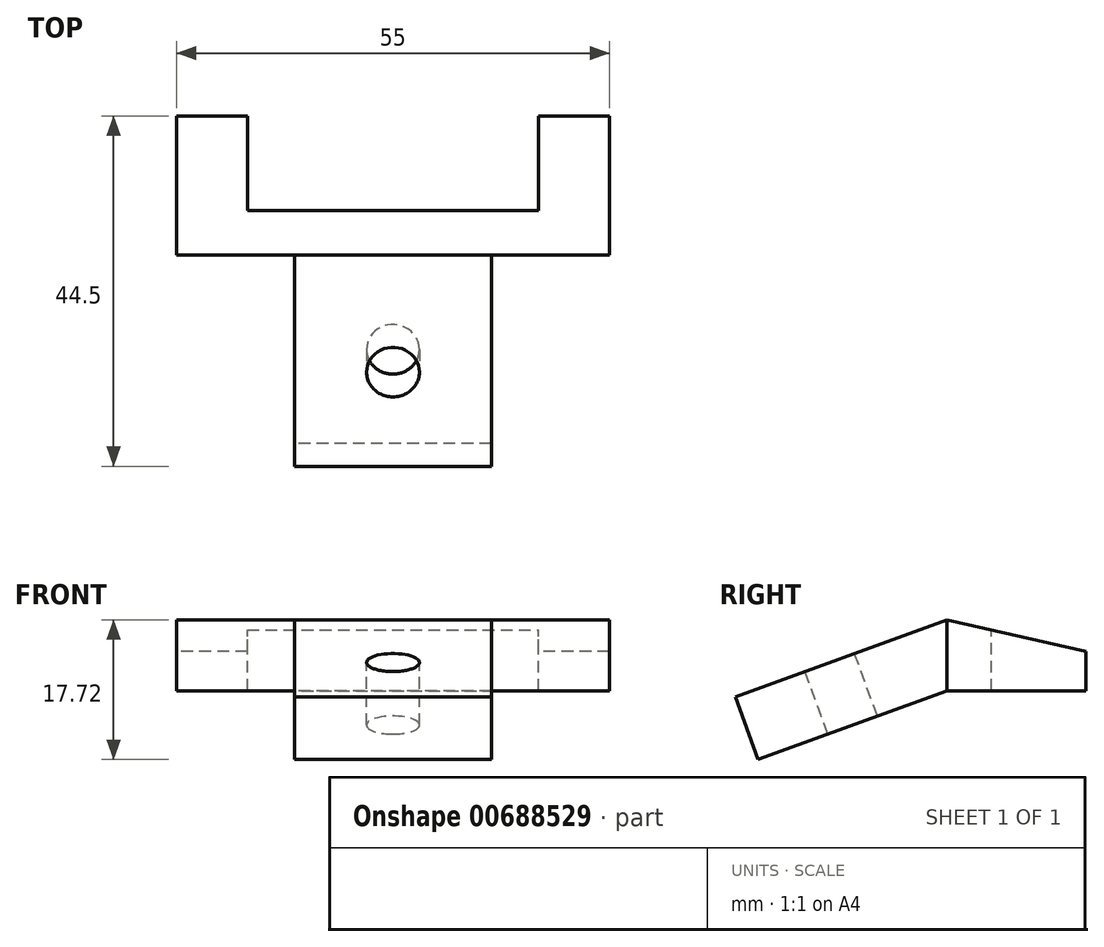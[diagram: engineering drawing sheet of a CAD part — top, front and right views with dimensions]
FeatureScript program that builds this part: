
annotation { "Feature Type Name" : "Feature", "Feature Type Description" : "" }
export const myFeature = defineFeature(function(context is Context, id is Id, definition is map)
    precondition{}
    {
        {
            var Q0;
            Q0=qCreatedBy(makeId("Right.planeOp"),FACE);
            var sketch = newSketch(context, id + "F0", { "sketchPlane" : qUnion([Q0])});
            skLineSegment(sketch, "E0", {"start": v(-3.63, 0) * mm, "end": v(14.02, 0) * mm});
            skLineSegment(sketch, "E1", {"start": v(14.02, 0) * mm, "end": v(14.02, 5) * mm});
            skLineSegment(sketch, "E2", {"start": v(14.02, 5) * mm, "end": v(-3.63, 9) * mm});
            skLineSegment(sketch, "E3", {"start": v(-27.59, -8.72) * mm, "end": v(-3.63, 0) * mm});
            skLineSegment(sketch, "E4", {"start": v(-27.59, -8.72) * mm, "end": v(-30.48, -0.77) * mm});
            skLineSegment(sketch, "E5", {"start": v(-30.48, -0.77) * mm, "end": v(-3.63, 9) * mm});
            skLineSegment(sketch, "E6", {"start": v(-27.59, -8.72) * mm, "end": v(-15.6, -4.36) * mm});
            skLineSegment(sketch, "E7", {"start": v(-15.6, -4.36) * mm, "end": v(-18.5, 3.59) * mm});
            skLineSegment(sketch, "E8", {"start": v(-3.63, 0) * mm, "end": v(-3.63, 9) * mm});
            skLineSegment(sketch, "E9.0", {"start": v(2.02, 0) * mm, "end": v(2.02, 7.72) * mm});
            skSolve(sketch);
        }
        {
            var Q0;
            {var subQ0=sQuery(id+"F0.wireOp",EDGE,"E1");Q0=makeQuery(id+"F0.imprint","IMPRINT",FACE,{"disambiguationData":[TD([[makeQuery(id+"F0.imprint","IMPRINT",EDGE,{"derivedFrom":subQ0}),1.0]])]});}
            var Q1;
            {var subQ0=sQuery(id+"F0.wireOp",EDGE,"E8");Q1=makeQuery(id+"F0.imprint","IMPRINT",FACE,{"disambiguationData":[TD([[makeQuery(id+"F0.imprint","IMPRINT",EDGE,{"derivedFrom":subQ0}),-1.0]])]});}
            extrude(context, id + "F1", {"entities" : qUnion([Q0, Q1]), "endBound" : BoundingType.SYMMETRIC, "depth" : 55 * mm, "offsetDistance" : 25 * mm});
        }
        {
            var Q0;
            Q0=makeQuery(id+"F0.imprint","IMPRINT",FACE,{"disambiguationData":[TD([[makeQuery(id+"F0.imprint","IMPRINT",EDGE,{"derivedFrom":sQuery(id+"F0.wireOp",EDGE,"E3")}),1.0]])]});
            var Q1;
            {var subQ0=sQuery(id+"F0.wireOp",EDGE,"E4");Q1=makeQuery(id+"F0.imprint","IMPRINT",FACE,{"disambiguationData":[TD([[makeQuery(id+"F0.imprint","IMPRINT",EDGE,{"derivedFrom":subQ0}),-1.0]])]});}
            extrude(context, id + "F2", {"entities" : qUnion([Q0, Q1]), "operationType" : NewBodyOperationType.ADD, "endBound" : BoundingType.SYMMETRIC, "depth" : 25 * mm, "offsetDistance" : 25 * mm});
        }
        {
            var Q0;
            {var subQ0=sQuery(id+"F0.wireOp",EDGE,"E1");Q0=makeQuery(id+"F0.imprint","IMPRINT",FACE,{"disambiguationData":[TD([[makeQuery(id+"F0.imprint","IMPRINT",EDGE,{"derivedFrom":subQ0}),1.0]])]});}
            extrude(context, id + "F3", {"entities" : qUnion([Q0]), "operationType" : NewBodyOperationType.REMOVE, "endBound" : BoundingType.SYMMETRIC, "oppositeDirection" : true, "depth" : 37 * mm, "offsetDistance" : 25 * mm});
        }
        {
            var Q0;
            Q0=makeQuery(id+"F2.opExtrude","SWEPT_FACE",FACE,{"disambiguationData":[OSD([sQuery(id+"F0.wireOp",EDGE,"E5")])]});
            var sketch = newSketch(context, id + "F4", { "sketchPlane" : qUnion([Q0])});
            skCircle(sketch, "E10", {"center": v(0, -16.16) * mm, "radius": 3.35 * mm});
            skSolve(sketch);
        }
        {
            var Q0;
            Q0=makeQuery(id+"F4.imprint","IMPRINT",FACE,{"disambiguationData":[TD([[makeQuery(id+"F4.imprint","IMPRINT",EDGE,{"derivedFrom":sQuery(id+"F4.wireOp",EDGE,"E10")}),1.0]])]});
            var Q1;
            Q1=sQuery(id+"F4.wireOp",EDGE,"E10");
            extrude(context, id + "F5", {"entities" : qUnion([Q0]), "operationType" : NewBodyOperationType.REMOVE, "surfaceEntities" : qUnion([Q1]), "endBound" : BoundingType.UP_TO_NEXT, "oppositeDirection" : true, "depth" : 25 * mm, "offsetDistance" : 25 * mm});
        }
    });
